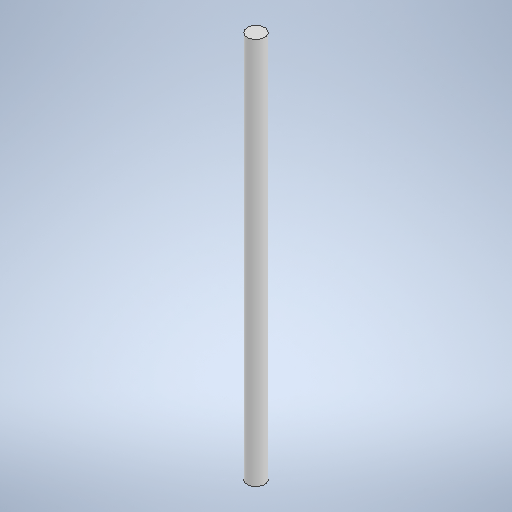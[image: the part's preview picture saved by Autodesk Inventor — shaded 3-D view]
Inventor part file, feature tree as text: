
AUTODESK INVENTOR PART (.ipt)
format: ipt  version: 2025.2 (Build 292293000, 293)  size: 234,496 bytes
history: native  units: mm
features: extrude x1, sketch x1
ambient origin geometry x8: Origin, YZ Plane, XZ Plane, XY Plane, X Axis, Y Axis, Z Axis, Center Point
bodies: Solid1 (feature_tree)
feature tree (2):
  extrude  "Extrusion1"  Depth=100.0mm TaperAngle=0.0deg
  sketch  "Sketch1"  dims[d0=4.5mm d1=100.0mm d2=0.0mm]
